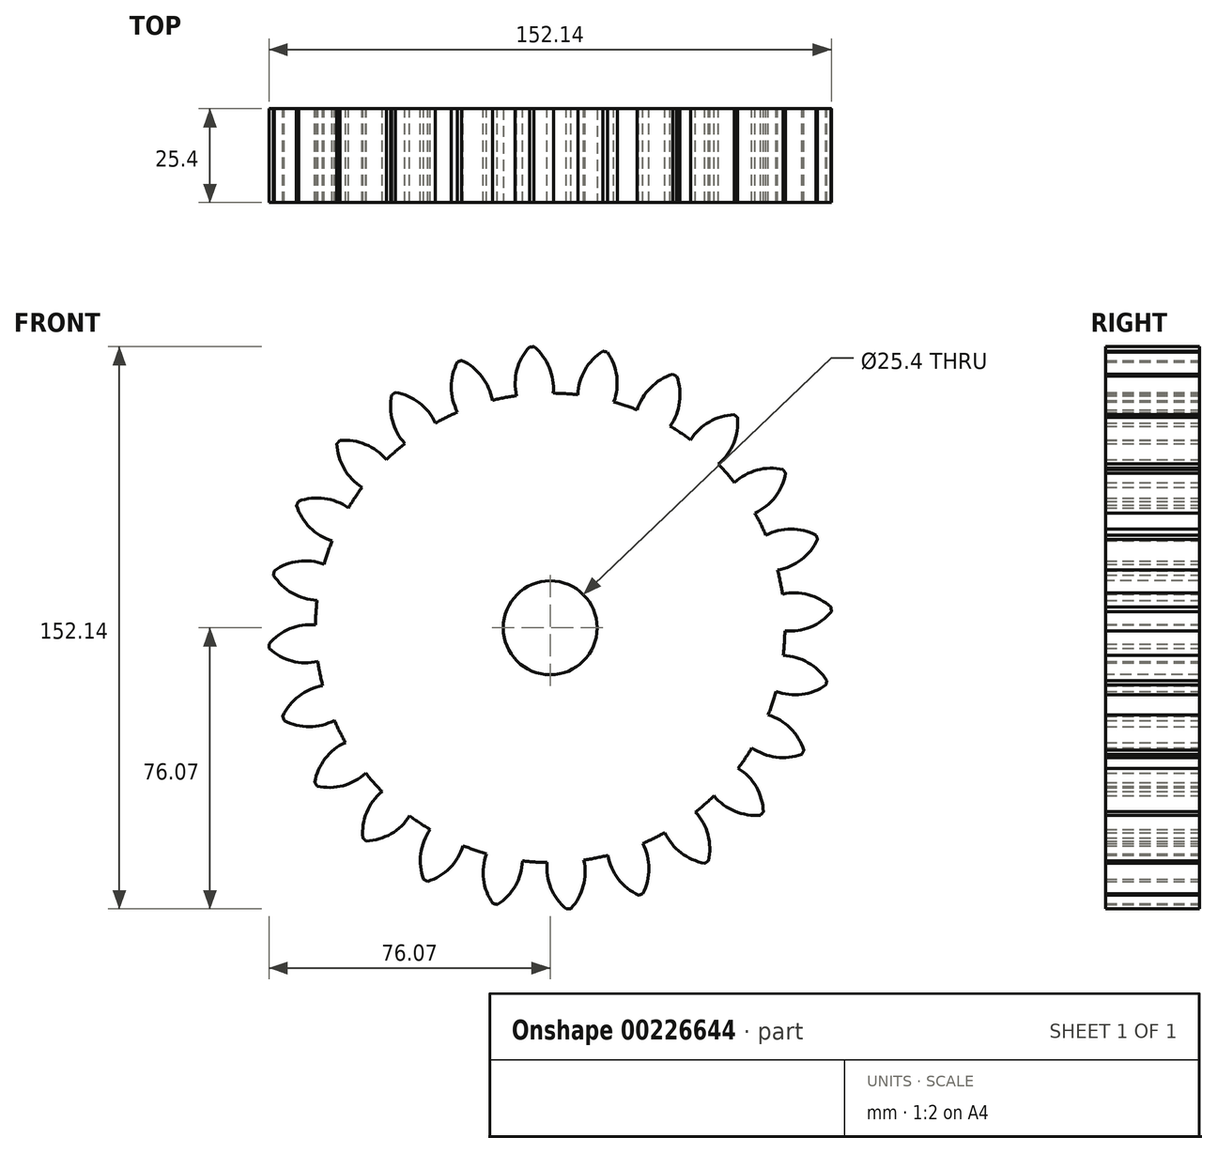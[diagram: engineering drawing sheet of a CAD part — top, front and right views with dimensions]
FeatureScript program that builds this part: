
annotation { "Feature Type Name" : "Feature", "Feature Type Description" : "" }
export const myFeature = defineFeature(function(context is Context, id is Id, definition is map)
    precondition{}
    {
        {
            var Q0;
            Q0=qCreatedBy(makeId("Front.planeOp"),FACE);
            var sketch = newSketch(context, id + "F0", { "sketchPlane" : qUnion([Q0])});
            skPoint(sketch, "E0.rect.middle", {"position": v(0, 0) * mm});
            skLineSegment(sketch, "E1", {"start": v(0, 0) * mm, "end": v(0, 76.2) * mm});
            skLineSegment(sketch, "E2", {"start": v(0, 0) * mm, "end": v(0, -76.2) * mm});
            skLineSegment(sketch, "E3", {"start": v(0, 0) * mm, "end": v(19.72, 73.6) * mm});
            skLineSegment(sketch, "E4", {"start": v(0, 0) * mm, "end": v(38.1, 66) * mm});
            skLineSegment(sketch, "E5", {"start": v(0, 0) * mm, "end": v(53.88, 53.88) * mm});
            skLineSegment(sketch, "E6", {"start": v(0, 0) * mm, "end": v(66, 38.1) * mm});
            skLineSegment(sketch, "E7", {"start": v(0, 0) * mm, "end": v(73.6, 19.72) * mm});
            skLineSegment(sketch, "E8", {"start": v(0, 0) * mm, "end": v(76.2, 0) * mm});
            skLineSegment(sketch, "E9", {"start": v(0, 0) * mm, "end": v(73.6, -19.72) * mm});
            skLineSegment(sketch, "E10", {"start": v(0, 0) * mm, "end": v(66, -38.1) * mm});
            skLineSegment(sketch, "E11", {"start": v(0, 0) * mm, "end": v(53.88, -53.88) * mm});
            skLineSegment(sketch, "E12", {"start": v(0, 0) * mm, "end": v(38.1, -66) * mm});
            skLineSegment(sketch, "E13", {"start": v(0, 0) * mm, "end": v(19.72, -73.6) * mm});
            skLineSegment(sketch, "E14", {"start": v(0, 0) * mm, "end": v(-19.72, -73.6) * mm});
            skLineSegment(sketch, "E15", {"start": v(0, 0) * mm, "end": v(-38.1, -66) * mm});
            skLineSegment(sketch, "E16", {"start": v(0, 0) * mm, "end": v(-53.88, -53.88) * mm});
            skLineSegment(sketch, "E17", {"start": v(0, 0) * mm, "end": v(-66, -38.1) * mm});
            skLineSegment(sketch, "E18", {"start": v(0, 0) * mm, "end": v(-73.6, -19.72) * mm});
            skLineSegment(sketch, "E19", {"start": v(0, 0) * mm, "end": v(-76.2, 0.07) * mm});
            skLineSegment(sketch, "E20", {"start": v(0, 0) * mm, "end": v(-73.6, 19.72) * mm});
            skLineSegment(sketch, "E21", {"start": v(0, 0) * mm, "end": v(-66, 38.1) * mm});
            skLineSegment(sketch, "E22", {"start": v(0, 0) * mm, "end": v(-53.88, 53.88) * mm});
            skLineSegment(sketch, "E23", {"start": v(0, 0) * mm, "end": v(-38.1, 66) * mm});
            skLineSegment(sketch, "E24", {"start": v(0, 0) * mm, "end": v(-19.72, 73.6) * mm});
            skCircle(sketch, "E25", {"center": v(0, 0) * mm, "radius": 76.2 * mm});
            skCircle(sketch, "E26", {"center": v(0, 0) * mm, "radius": 69.85 * mm});
            skCircle(sketch, "E27", {"center": v(0, 0) * mm, "radius": 63.5 * mm});
            skLineSegment(sketch, "E28", {"start": v(0, 0) * mm, "end": v(-4.98, 76.04) * mm});
            skLineSegment(sketch, "E29", {"start": v(0, 69.85) * mm, "end": v(-76.58, 69.85) * mm});
            skLineSegment(sketch, "E30", {"start": v(0, 69.85) * mm, "end": v(-76.5, 42) * mm});
            skLineSegment(sketch, "E31", {"start": v(-4.98, 76.04) * mm, "end": v(-7.15, 109.16) * mm});
            skLineSegment(sketch, "E32", {"start": v(0, 76.2) * mm, "end": v(0, 110.22) * mm});
            skCircle(sketch, "E33", {"center": v(0, 69.85) * mm, "radius": 14.6 * mm});
            skPoint(sketch, "E34", {"position": v(-13.72, 64.85) * mm});
            skArc(sketch, "E35", {"start": v(0.82, 63.5) * mm, "mid": v(-0.22, 70.43) * mm, "end": v(-4.37, 76.07) * mm});
            skArc(sketch, "E36.MirrorCS", {"start": v(-9.1, 62.84) * mm, "mid": v(-8.97, 69.85) * mm, "end": v(-5.6, 76) * mm});
            skSolve(sketch);
        }
        {
            var Q0;
            {var subQ1=sQuery(id+"F0.wireOp",EDGE,"E23");var subQ3=sQuery(id+"F0.wireOp",EDGE,"E27");var subQ4=makeQuery(id+"F0.imprint","INTERSECT",VERTEX,{"derivedFrom":[subQ1,subQ3]});Q0=makeQuery(id+"F0.imprint","IMPRINT",FACE,{"disambiguationData":[TD([[makeQuery(id+"F0.imprint","IMPRINT",EDGE,{"disambiguationData":[TD([[subQ4,1.0]])],"derivedFrom":subQ3}),1.0]])]});}
            var Q1;
            {var subQ1=sQuery(id+"F0.wireOp",EDGE,"E22");var subQ3=sQuery(id+"F0.wireOp",EDGE,"E27");var subQ4=makeQuery(id+"F0.imprint","INTERSECT",VERTEX,{"derivedFrom":[subQ1,subQ3]});Q1=makeQuery(id+"F0.imprint","IMPRINT",FACE,{"disambiguationData":[TD([[makeQuery(id+"F0.imprint","IMPRINT",EDGE,{"disambiguationData":[TD([[subQ4,1.0]])],"derivedFrom":subQ3}),1.0]])]});}
            var Q2;
            {var subQ1=sQuery(id+"F0.wireOp",EDGE,"E1");var subQ3=sQuery(id+"F0.wireOp",EDGE,"E33");var subQ4=makeQuery(id+"F0.imprint","INTERSECT",VERTEX,{"derivedFrom":[subQ1,subQ3]});Q2=makeQuery(id+"F0.imprint","IMPRINT",FACE,{"disambiguationData":[TD([[makeQuery(id+"F0.imprint","IMPRINT",EDGE,{"disambiguationData":[TD([[subQ4,1.0]])],"derivedFrom":subQ3}),-1.0]])]});}
            var Q3;
            {var subQ1=sQuery(id+"F0.wireOp",EDGE,"E19");var subQ3=sQuery(id+"F0.wireOp",EDGE,"E27");var subQ4=makeQuery(id+"F0.imprint","INTERSECT",VERTEX,{"derivedFrom":[subQ1,subQ3]});Q3=makeQuery(id+"F0.imprint","IMPRINT",FACE,{"disambiguationData":[TD([[makeQuery(id+"F0.imprint","IMPRINT",EDGE,{"disambiguationData":[TD([[subQ4,1.0]])],"derivedFrom":subQ3}),1.0]])]});}
            var Q4;
            {var subQ1=sQuery(id+"F0.wireOp",EDGE,"E24");var subQ3=sQuery(id+"F0.wireOp",EDGE,"E27");var subQ4=makeQuery(id+"F0.imprint","INTERSECT",VERTEX,{"derivedFrom":[subQ1,subQ3]});Q4=makeQuery(id+"F0.imprint","IMPRINT",FACE,{"disambiguationData":[TD([[makeQuery(id+"F0.imprint","IMPRINT",EDGE,{"disambiguationData":[TD([[subQ4,1.0]])],"derivedFrom":subQ3}),1.0]])]});}
            var Q5;
            {var subQ1=sQuery(id+"F0.wireOp",EDGE,"E20");var subQ3=sQuery(id+"F0.wireOp",EDGE,"E27");var subQ4=makeQuery(id+"F0.imprint","INTERSECT",VERTEX,{"derivedFrom":[subQ1,subQ3]});Q5=makeQuery(id+"F0.imprint","IMPRINT",FACE,{"disambiguationData":[TD([[makeQuery(id+"F0.imprint","IMPRINT",EDGE,{"disambiguationData":[TD([[subQ4,1.0]])],"derivedFrom":subQ3}),1.0]])]});}
            var Q6;
            {var subQ1=sQuery(id+"F0.wireOp",EDGE,"E21");var subQ3=sQuery(id+"F0.wireOp",EDGE,"E27");var subQ4=makeQuery(id+"F0.imprint","INTERSECT",VERTEX,{"derivedFrom":[subQ1,subQ3]});Q6=makeQuery(id+"F0.imprint","IMPRINT",FACE,{"disambiguationData":[TD([[makeQuery(id+"F0.imprint","IMPRINT",EDGE,{"disambiguationData":[TD([[subQ4,1.0]])],"derivedFrom":subQ3}),1.0]])]});}
            var Q7;
            {var subQ1=sQuery(id+"F0.wireOp",EDGE,"E6");var subQ3=sQuery(id+"F0.wireOp",EDGE,"E27");var subQ4=makeQuery(id+"F0.imprint","INTERSECT",VERTEX,{"derivedFrom":[subQ1,subQ3]});Q7=makeQuery(id+"F0.imprint","IMPRINT",FACE,{"disambiguationData":[TD([[makeQuery(id+"F0.imprint","IMPRINT",EDGE,{"disambiguationData":[TD([[subQ4,1.0]])],"derivedFrom":subQ3}),1.0]])]});}
            var Q8;
            {var subQ1=sQuery(id+"F0.wireOp",EDGE,"E4");var subQ3=sQuery(id+"F0.wireOp",EDGE,"E27");var subQ4=makeQuery(id+"F0.imprint","INTERSECT",VERTEX,{"derivedFrom":[subQ1,subQ3]});Q8=makeQuery(id+"F0.imprint","IMPRINT",FACE,{"disambiguationData":[TD([[makeQuery(id+"F0.imprint","IMPRINT",EDGE,{"disambiguationData":[TD([[subQ4,1.0]])],"derivedFrom":subQ3}),1.0]])]});}
            var Q9;
            {var subQ1=sQuery(id+"F0.wireOp",EDGE,"E7");var subQ3=sQuery(id+"F0.wireOp",EDGE,"E27");var subQ4=makeQuery(id+"F0.imprint","INTERSECT",VERTEX,{"derivedFrom":[subQ1,subQ3]});Q9=makeQuery(id+"F0.imprint","IMPRINT",FACE,{"disambiguationData":[TD([[makeQuery(id+"F0.imprint","IMPRINT",EDGE,{"disambiguationData":[TD([[subQ4,1.0]])],"derivedFrom":subQ3}),1.0]])]});}
            var Q10;
            {var subQ0=sQuery(id+"F0.wireOp",EDGE,"E3");var subQ5=sQuery(id+"F0.wireOp",EDGE,"E27");var subQ6=makeQuery(id+"F0.imprint","INTERSECT",VERTEX,{"derivedFrom":[subQ0,subQ5]});Q10=makeQuery(id+"F0.imprint","IMPRINT",FACE,{"disambiguationData":[TD([[makeQuery(id+"F0.imprint","IMPRINT",EDGE,{"disambiguationData":[TD([[subQ6,-1.0]])],"derivedFrom":subQ5}),1.0]])]});}
            var Q11;
            {var subQ1=sQuery(id+"F0.wireOp",EDGE,"E3");var subQ3=sQuery(id+"F0.wireOp",EDGE,"E27");var subQ4=makeQuery(id+"F0.imprint","INTERSECT",VERTEX,{"derivedFrom":[subQ1,subQ3]});Q11=makeQuery(id+"F0.imprint","IMPRINT",FACE,{"disambiguationData":[TD([[makeQuery(id+"F0.imprint","IMPRINT",EDGE,{"disambiguationData":[TD([[subQ4,1.0]])],"derivedFrom":subQ3}),1.0]])]});}
            var Q12;
            {var subQ1=sQuery(id+"F0.wireOp",EDGE,"E5");var subQ3=sQuery(id+"F0.wireOp",EDGE,"E27");var subQ4=makeQuery(id+"F0.imprint","INTERSECT",VERTEX,{"derivedFrom":[subQ1,subQ3]});Q12=makeQuery(id+"F0.imprint","IMPRINT",FACE,{"disambiguationData":[TD([[makeQuery(id+"F0.imprint","IMPRINT",EDGE,{"disambiguationData":[TD([[subQ4,1.0]])],"derivedFrom":subQ3}),1.0]])]});}
            var Q13;
            {var subQ1=sQuery(id+"F0.wireOp",EDGE,"E17");var subQ3=sQuery(id+"F0.wireOp",EDGE,"E27");var subQ4=makeQuery(id+"F0.imprint","INTERSECT",VERTEX,{"derivedFrom":[subQ1,subQ3]});Q13=makeQuery(id+"F0.imprint","IMPRINT",FACE,{"disambiguationData":[TD([[makeQuery(id+"F0.imprint","IMPRINT",EDGE,{"disambiguationData":[TD([[subQ4,1.0]])],"derivedFrom":subQ3}),1.0]])]});}
            var Q14;
            {var subQ1=sQuery(id+"F0.wireOp",EDGE,"E15");var subQ3=sQuery(id+"F0.wireOp",EDGE,"E27");var subQ4=makeQuery(id+"F0.imprint","INTERSECT",VERTEX,{"derivedFrom":[subQ1,subQ3]});Q14=makeQuery(id+"F0.imprint","IMPRINT",FACE,{"disambiguationData":[TD([[makeQuery(id+"F0.imprint","IMPRINT",EDGE,{"disambiguationData":[TD([[subQ4,1.0]])],"derivedFrom":subQ3}),1.0]])]});}
            var Q15;
            {var subQ1=sQuery(id+"F0.wireOp",EDGE,"E16");var subQ3=sQuery(id+"F0.wireOp",EDGE,"E27");var subQ4=makeQuery(id+"F0.imprint","INTERSECT",VERTEX,{"derivedFrom":[subQ1,subQ3]});Q15=makeQuery(id+"F0.imprint","IMPRINT",FACE,{"disambiguationData":[TD([[makeQuery(id+"F0.imprint","IMPRINT",EDGE,{"disambiguationData":[TD([[subQ4,1.0]])],"derivedFrom":subQ3}),1.0]])]});}
            var Q16;
            {var subQ1=sQuery(id+"F0.wireOp",EDGE,"E2");var subQ3=sQuery(id+"F0.wireOp",EDGE,"E27");var subQ4=makeQuery(id+"F0.imprint","INTERSECT",VERTEX,{"derivedFrom":[subQ1,subQ3]});Q16=makeQuery(id+"F0.imprint","IMPRINT",FACE,{"disambiguationData":[TD([[makeQuery(id+"F0.imprint","IMPRINT",EDGE,{"disambiguationData":[TD([[subQ4,1.0]])],"derivedFrom":subQ3}),1.0]])]});}
            var Q17;
            {var subQ1=sQuery(id+"F0.wireOp",EDGE,"E14");var subQ3=sQuery(id+"F0.wireOp",EDGE,"E27");var subQ4=makeQuery(id+"F0.imprint","INTERSECT",VERTEX,{"derivedFrom":[subQ1,subQ3]});Q17=makeQuery(id+"F0.imprint","IMPRINT",FACE,{"disambiguationData":[TD([[makeQuery(id+"F0.imprint","IMPRINT",EDGE,{"disambiguationData":[TD([[subQ4,1.0]])],"derivedFrom":subQ3}),1.0]])]});}
            var Q18;
            {var subQ1=sQuery(id+"F0.wireOp",EDGE,"E18");var subQ3=sQuery(id+"F0.wireOp",EDGE,"E27");var subQ4=makeQuery(id+"F0.imprint","INTERSECT",VERTEX,{"derivedFrom":[subQ1,subQ3]});Q18=makeQuery(id+"F0.imprint","IMPRINT",FACE,{"disambiguationData":[TD([[makeQuery(id+"F0.imprint","IMPRINT",EDGE,{"disambiguationData":[TD([[subQ4,1.0]])],"derivedFrom":subQ3}),1.0]])]});}
            var Q19;
            {var subQ0=sQuery(id+"F0.wireOp",EDGE,"E33");var subQ1=sQuery(id+"F0.wireOp",EDGE,"E1");var subQ2=makeQuery(id+"F0.imprint","INTERSECT",VERTEX,{"derivedFrom":[subQ1,subQ0]});Q19=makeQuery(id+"F0.imprint","IMPRINT",FACE,{"disambiguationData":[TD([[makeQuery(id+"F0.imprint","IMPRINT",EDGE,{"disambiguationData":[TD([[subQ2,-1.0]])],"derivedFrom":subQ1}),1.0]])]});}
            var Q20;
            {var subQ0=sQuery(id+"F0.wireOp",EDGE,"E27");var subQ1=makeQuery(id+"F0.imprint","INTERSECT",VERTEX,{"derivedFrom":[subQ0,sQuery(id+"F0.wireOp",EDGE,"E36.MirrorCS")]});Q20=makeQuery(id+"F0.imprint","IMPRINT",FACE,{"disambiguationData":[TD([[makeQuery(id+"F0.imprint","IMPRINT",EDGE,{"disambiguationData":[TD([[subQ1,1.0]])],"derivedFrom":subQ0}),1.0]])]});}
            var Q21;
            {var subQ0=sQuery(id+"F0.wireOp",EDGE,"E33");var subQ1=sQuery(id+"F0.wireOp",EDGE,"E1");var subQ2=makeQuery(id+"F0.imprint","INTERSECT",VERTEX,{"derivedFrom":[subQ1,subQ0]});Q21=makeQuery(id+"F0.imprint","IMPRINT",FACE,{"disambiguationData":[TD([[makeQuery(id+"F0.imprint","IMPRINT",EDGE,{"disambiguationData":[TD([[subQ2,-1.0]])],"derivedFrom":subQ1}),-1.0]])]});}
            var Q22;
            {var subQ1=sQuery(id+"F0.wireOp",EDGE,"E1");var subQ3=sQuery(id+"F0.wireOp",EDGE,"E27");var subQ4=makeQuery(id+"F0.imprint","INTERSECT",VERTEX,{"derivedFrom":[subQ1,subQ3]});Q22=makeQuery(id+"F0.imprint","IMPRINT",FACE,{"disambiguationData":[TD([[makeQuery(id+"F0.imprint","IMPRINT",EDGE,{"disambiguationData":[TD([[subQ4,-1.0]])],"derivedFrom":subQ3}),-1.0]])]});}
            var Q23;
            {var subQ0=sQuery(id+"F0.wireOp",EDGE,"E36.MirrorCS");var subQ1=sQuery(id+"F0.wireOp",EDGE,"E27");var subQ2=makeQuery(id+"F0.imprint","INTERSECT",VERTEX,{"derivedFrom":[subQ1,subQ0]});Q23=makeQuery(id+"F0.imprint","IMPRINT",FACE,{"disambiguationData":[TD([[makeQuery(id+"F0.imprint","IMPRINT",EDGE,{"disambiguationData":[TD([[subQ2,1.0]])],"derivedFrom":subQ1}),-1.0]])]});}
            var Q24;
            {var subQ0=sQuery(id+"F0.wireOp",EDGE,"E28");var subQ1=sQuery(id+"F0.wireOp",EDGE,"E26");var subQ2=makeQuery(id+"F0.imprint","INTERSECT",VERTEX,{"derivedFrom":[subQ1,subQ0]});Q24=makeQuery(id+"F0.imprint","IMPRINT",FACE,{"disambiguationData":[TD([[makeQuery(id+"F0.imprint","IMPRINT",EDGE,{"disambiguationData":[TD([[subQ2,-1.0]])],"derivedFrom":subQ1}),1.0]])]});}
            var Q25;
            {var subQ0=sQuery(id+"F0.wireOp",EDGE,"E28");var subQ1=sQuery(id+"F0.wireOp",EDGE,"E26");var subQ2=makeQuery(id+"F0.imprint","INTERSECT",VERTEX,{"derivedFrom":[subQ1,subQ0]});Q25=makeQuery(id+"F0.imprint","IMPRINT",FACE,{"disambiguationData":[TD([[makeQuery(id+"F0.imprint","IMPRINT",EDGE,{"disambiguationData":[TD([[subQ2,-1.0]])],"derivedFrom":subQ1}),-1.0]])]});}
            var Q26;
            {var subQ0=sQuery(id+"F0.wireOp",EDGE,"E28");var subQ5=sQuery(id+"F0.wireOp",EDGE,"E29");var subQ6=makeQuery(id+"F0.imprint","INTERSECT",VERTEX,{"derivedFrom":[subQ0,subQ5]});Q26=makeQuery(id+"F0.imprint","IMPRINT",FACE,{"disambiguationData":[TD([[makeQuery(id+"F0.imprint","IMPRINT",EDGE,{"disambiguationData":[TD([[subQ6,-1.0]])],"derivedFrom":subQ5}),-1.0]])]});}
            var Q27;
            {var subQ1=sQuery(id+"F0.wireOp",EDGE,"E25");var subQ3=sQuery(id+"F0.wireOp",EDGE,"E35");var subQ4=makeQuery(id+"F0.imprint","INTERSECT",VERTEX,{"derivedFrom":[subQ1,subQ3]});Q27=makeQuery(id+"F0.imprint","IMPRINT",FACE,{"disambiguationData":[TD([[makeQuery(id+"F0.imprint","IMPRINT",EDGE,{"disambiguationData":[TD([[subQ4,-1.0]])],"derivedFrom":subQ1}),1.0]])]});}
            var Q28;
            {var subQ0=sQuery(id+"F0.wireOp",EDGE,"E35");var subQ3=sQuery(id+"F0.wireOp",EDGE,"E27");var subQ5=makeQuery(id+"F0.imprint","INTERSECT",VERTEX,{"derivedFrom":[subQ3,subQ0]});Q28=makeQuery(id+"F0.imprint","IMPRINT",FACE,{"disambiguationData":[TD([[makeQuery(id+"F0.imprint","IMPRINT",EDGE,{"disambiguationData":[TD([[subQ5,-1.0]])],"derivedFrom":subQ3}),-1.0]])]});}
            var Q29;
            {var subQ1=sQuery(id+"F0.wireOp",EDGE,"E26");var subQ3=sQuery(id+"F0.wireOp",EDGE,"E28");var subQ4=makeQuery(id+"F0.imprint","INTERSECT",VERTEX,{"derivedFrom":[subQ1,subQ3]});Q29=makeQuery(id+"F0.imprint","IMPRINT",FACE,{"disambiguationData":[TD([[makeQuery(id+"F0.imprint","IMPRINT",EDGE,{"disambiguationData":[TD([[subQ4,-1.0]])],"derivedFrom":subQ3}),-1.0]])]});}
            var Q30;
            {var subQ1=sQuery(id+"F0.wireOp",EDGE,"E26");var subQ3=sQuery(id+"F0.wireOp",EDGE,"E28");var subQ4=makeQuery(id+"F0.imprint","INTERSECT",VERTEX,{"derivedFrom":[subQ1,subQ3]});Q30=makeQuery(id+"F0.imprint","IMPRINT",FACE,{"disambiguationData":[TD([[makeQuery(id+"F0.imprint","IMPRINT",EDGE,{"disambiguationData":[TD([[subQ4,1.0]])],"derivedFrom":subQ3}),-1.0]])]});}
            var Q31;
            {var subQ1=sQuery(id+"F0.wireOp",EDGE,"E10");var subQ3=sQuery(id+"F0.wireOp",EDGE,"E27");var subQ4=makeQuery(id+"F0.imprint","INTERSECT",VERTEX,{"derivedFrom":[subQ1,subQ3]});Q31=makeQuery(id+"F0.imprint","IMPRINT",FACE,{"disambiguationData":[TD([[makeQuery(id+"F0.imprint","IMPRINT",EDGE,{"disambiguationData":[TD([[subQ4,1.0]])],"derivedFrom":subQ3}),1.0]])]});}
            var Q32;
            {var subQ1=sQuery(id+"F0.wireOp",EDGE,"E9");var subQ3=sQuery(id+"F0.wireOp",EDGE,"E27");var subQ4=makeQuery(id+"F0.imprint","INTERSECT",VERTEX,{"derivedFrom":[subQ1,subQ3]});Q32=makeQuery(id+"F0.imprint","IMPRINT",FACE,{"disambiguationData":[TD([[makeQuery(id+"F0.imprint","IMPRINT",EDGE,{"disambiguationData":[TD([[subQ4,1.0]])],"derivedFrom":subQ3}),1.0]])]});}
            var Q33;
            {var subQ1=sQuery(id+"F0.wireOp",EDGE,"E8");var subQ3=sQuery(id+"F0.wireOp",EDGE,"E27");var subQ4=makeQuery(id+"F0.imprint","INTERSECT",VERTEX,{"derivedFrom":[subQ1,subQ3]});Q33=makeQuery(id+"F0.imprint","IMPRINT",FACE,{"disambiguationData":[TD([[makeQuery(id+"F0.imprint","IMPRINT",EDGE,{"disambiguationData":[TD([[subQ4,1.0]])],"derivedFrom":subQ3}),1.0]])]});}
            var Q34;
            {var subQ1=sQuery(id+"F0.wireOp",EDGE,"E11");var subQ3=sQuery(id+"F0.wireOp",EDGE,"E27");var subQ4=makeQuery(id+"F0.imprint","INTERSECT",VERTEX,{"derivedFrom":[subQ1,subQ3]});Q34=makeQuery(id+"F0.imprint","IMPRINT",FACE,{"disambiguationData":[TD([[makeQuery(id+"F0.imprint","IMPRINT",EDGE,{"disambiguationData":[TD([[subQ4,1.0]])],"derivedFrom":subQ3}),1.0]])]});}
            var Q35;
            {var subQ1=sQuery(id+"F0.wireOp",EDGE,"E2");var subQ3=sQuery(id+"F0.wireOp",EDGE,"E27");var subQ4=makeQuery(id+"F0.imprint","INTERSECT",VERTEX,{"derivedFrom":[subQ1,subQ3]});Q35=makeQuery(id+"F0.imprint","IMPRINT",FACE,{"disambiguationData":[TD([[makeQuery(id+"F0.imprint","IMPRINT",EDGE,{"disambiguationData":[TD([[subQ4,-1.0]])],"derivedFrom":subQ3}),1.0]])]});}
            var Q36;
            {var subQ1=sQuery(id+"F0.wireOp",EDGE,"E12");var subQ3=sQuery(id+"F0.wireOp",EDGE,"E27");var subQ4=makeQuery(id+"F0.imprint","INTERSECT",VERTEX,{"derivedFrom":[subQ1,subQ3]});Q36=makeQuery(id+"F0.imprint","IMPRINT",FACE,{"disambiguationData":[TD([[makeQuery(id+"F0.imprint","IMPRINT",EDGE,{"disambiguationData":[TD([[subQ4,1.0]])],"derivedFrom":subQ3}),1.0]])]});}
            extrude(context, id + "F1", {"entities" : qUnion([Q0, Q1, Q2, Q3, Q4, Q5, Q6, Q7, Q8, Q9, Q10, Q11, Q12, Q13, Q14, Q15, Q16, Q17, Q18, Q19, Q20, Q21, Q22, Q23, Q24, Q25, Q26, Q27, Q28, Q29, Q30, Q31, Q32, Q33, Q34, Q35, Q36]), "endBound" : BoundingType.SYMMETRIC, "depth" : 25.4 * mm});
        }
        {
            var Q0;
            Q0=makeQuery(id+"F1.opExtrude","SWEPT_BODY",BODY,{"disambiguationData":[OSD([sQuery(id+"F0.wireOp",EDGE,"E25"),sQuery(id+"F0.wireOp",EDGE,"E27"),sQuery(id+"F0.wireOp",EDGE,"E35"),sQuery(id+"F0.wireOp",EDGE,"E36.MirrorCS")])]});
            var Q1;
            Q1=makeQuery(id+"F1.opExtrude","SWEPT_FACE",FACE,{"disambiguationData":[OSD([sQuery(id+"F0.wireOp",EDGE,"E27")])]});
            circularPattern(context, id + "F2", {"operationType" : NewBodyOperationType.ADD, "entities" : qUnion([Q0]), "axis" : qUnion([Q1]), "angle" : 15 * degree, "instanceCount" : 24});
        }
        {
            var Q0;
            Q0=makeQuery(id+"F1.opExtrude","CAP_FACE",FACE,{"disambiguationData":[OSD([sQuery(id+"F0.wireOp",EDGE,"E25"),sQuery(id+"F0.wireOp",EDGE,"E27"),sQuery(id+"F0.wireOp",EDGE,"E35"),sQuery(id+"F0.wireOp",EDGE,"E36.MirrorCS")])],"isStart":false});
            var sketch = newSketch(context, id + "F3", { "sketchPlane" : qUnion([Q0])});
            skPoint(sketch, "E37", {"position": v(0, 0) * mm});
            skSolve(sketch);
        }
        {
            var Q0;
            Q0=sQuery(id+"F3.wireOp",VERTEX,"E37");
            var Q1;
            Q1=makeQuery(id+"F1.opExtrude","SWEPT_BODY",BODY,{"disambiguationData":[OSD([sQuery(id+"F0.wireOp",EDGE,"E25"),sQuery(id+"F0.wireOp",EDGE,"E27"),sQuery(id+"F0.wireOp",EDGE,"E35"),sQuery(id+"F0.wireOp",EDGE,"E36.MirrorCS")])]});
            hole(context, id + "F4", {"style" : HoleStyle.SIMPLE, "holeDiameter" : 25.4 * mm, "endStyle" : HoleEndStyle.THROUGH, "locations" : qUnion([Q0]), "scope" : qUnion([Q1]), "isTappedThrough" : true});
        }
    });
